# Revit family: Lyraplus washbasin 40X31 cm mounting skrews
name_source: partatom
category: Plumbing Fixtures
units: mm (PartAtom-declared; Revit-internal decimal feet)

## family parameters
Always vertical = Yes
Cut with Voids When Loaded = No
Host = Wall
Part Type = Normal
Room Calculation Point = No
Round Connector Dimension = Use Diameter
Shared = No

## types (1)
- Lyraplus washbasin 40X31 cm mounting skrews
    Article Number = SAR1180
    BIMobject Category = Sanitary
    BIMobject QR code url = http://jika-fi.bimobject.com
    Date of publishing = 6/11/2012
    Default Elevation = 0 mm  [stored 0 ft]
    Depth (mm) = 310 mm
    Design country = Czech Republic
    Edition number = 1
    Height (mm) = 145 mm
    IFC Classification = Furnishing Element
    Manufacture country = Czech Republic
    Manufacturer = Jika-FI
    Manufacturer URL = http://www.laattapiste.fi
    Material main = Porcelain
    Material secondary = Stainless Steel AISI 304
    Model = Lyraplus washbasin 40X31 cm, taphole on right, white incl. mounting skrews
    NBS Reference = 35-65-70-94
    NBS Reference Description = Wash Basin Systems
    Name of the object = Lyraplus washbasin 40X31 cm, taphole on right, white incl. mounting skrews
    Product SKU = SAR1180
    Product data url = http://www.jika.eu
    Product family = Lyraplus
    Product group = Basins
    UNSPC Category = Sanitary ware
    UNSPC code = 301815
    URL = http://jika-fi.bimobject.com
    Uniclass 1.4 Code = L7212
    Uniclass 1.4 Description = Washbasins
    Uniclass 2.0 Code = SS-35-65-70-94
    Uniclass 2.0 Description = Wash Basin Systems
    Weight Net (kg) = 0 mm  [stored 0 ft]
    Width (mm) = 400 mm

note: [stored X ft] marks values corroborated as IEEE doubles in the binary element streams (Revit-internal decimal feet)

## geometry (parser evidence)
native form markers: Blend x6, Sweep x5
no freeform markers — native parametric forms only
